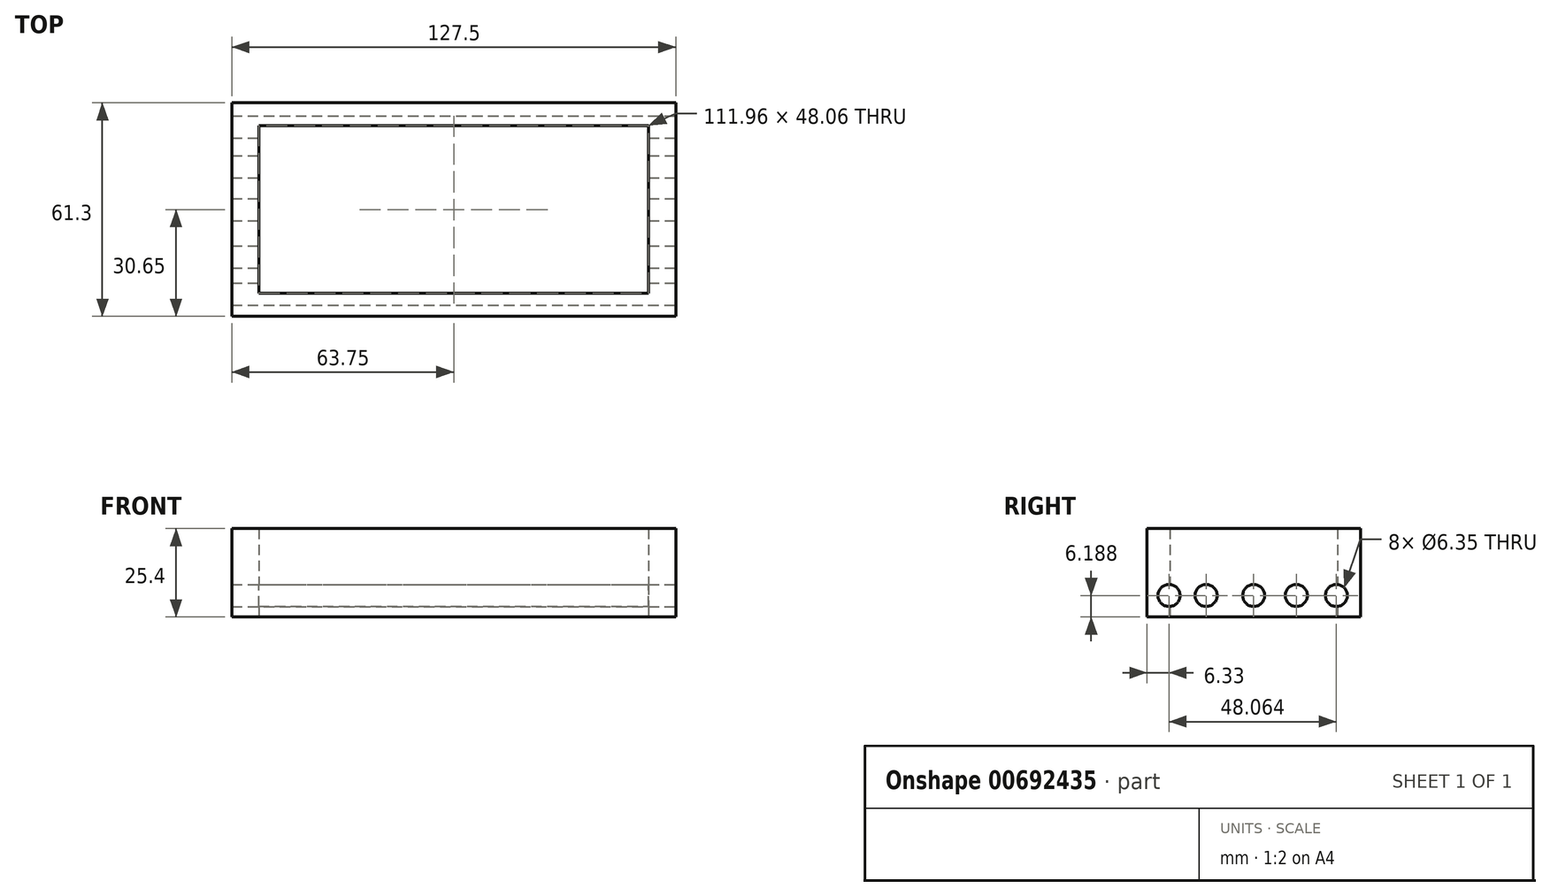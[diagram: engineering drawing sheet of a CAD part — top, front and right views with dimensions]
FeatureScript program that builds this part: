
annotation { "Feature Type Name" : "Feature", "Feature Type Description" : "" }
export const myFeature = defineFeature(function(context is Context, id is Id, definition is map)
    precondition{}
    {
        {
            var Q0;
            Q0=qCreatedBy(makeId("Top.planeOp"),FACE);
            var sketch = newSketch(context, id + "F0", { "sketchPlane" : qUnion([Q0])});
            skLineSegment(sketch, "E0.bottom", {"start": v(-63.75, 30.65) * mm, "end": v(63.75, 30.65) * mm});
            skLineSegment(sketch, "E0.top", {"start": v(-63.75, -30.65) * mm, "end": v(63.75, -30.65) * mm});
            skLineSegment(sketch, "E0.left", {"start": v(-63.75, 30.65) * mm, "end": v(-63.75, -30.65) * mm});
            skLineSegment(sketch, "E0.right", {"start": v(63.75, 30.65) * mm, "end": v(63.75, -30.65) * mm});
            skPoint(sketch, "E0.middle", {"position": v(0, 0) * mm});
            skLineSegment(sketch, "E1.bottom", {"start": v(-55.98, 24.03) * mm, "end": v(55.98, 24.03) * mm});
            skLineSegment(sketch, "E1.top", {"start": v(-55.98, -24.03) * mm, "end": v(55.98, -24.03) * mm});
            skLineSegment(sketch, "E1.left", {"start": v(-55.98, 24.03) * mm, "end": v(-55.98, -24.03) * mm});
            skLineSegment(sketch, "E1.right", {"start": v(55.98, 24.03) * mm, "end": v(55.98, -24.03) * mm});
            skSolve(sketch);
        }
        {
            var Q0;
            Q0=makeQuery(id+"F0.imprint","IMPRINT",FACE,{"disambiguationData":[TD([[makeQuery(id+"F0.imprint","IMPRINT",EDGE,{"derivedFrom":sQuery(id+"F0.wireOp",EDGE,"E0.bottom")}),-1.0]])]});
            extrude(context, id + "F1", {"entities" : qUnion([Q0]), "depth" : 25.4 * mm, "offsetDistance" : 25.4 * mm});
        }
        {
            var Q0;
            Q0=makeQuery(id+"F1.opExtrude","SWEPT_FACE",FACE,{"disambiguationData":[OSD([sQuery(id+"F0.wireOp",EDGE,"E0.right")])]});
            var sketch = newSketch(context, id + "F2", { "sketchPlane" : qUnion([Q0])});
            skPoint(sketch, "E2", {"position": v(-24.32, 6.19) * mm});
            skPoint(sketch, "E3", {"position": v(-13.67, 6.19) * mm});
            skPoint(sketch, "E4", {"position": v(0, 6.19) * mm});
            skPoint(sketch, "E5", {"position": v(12.23, 6.19) * mm});
            skPoint(sketch, "E6", {"position": v(23.74, 6.19) * mm});
            skSolve(sketch);
        }
        {
            var Q0;
            Q0=sQuery(id+"F2.wireOp",VERTEX,"E2");
            var Q1;
            Q1=sQuery(id+"F2.wireOp",VERTEX,"E3");
            var Q2;
            Q2=sQuery(id+"F2.wireOp",VERTEX,"E4");
            var Q3;
            Q3=sQuery(id+"F2.wireOp",VERTEX,"E5");
            var Q4;
            Q4=sQuery(id+"F2.wireOp",VERTEX,"E6");
            var Q5;
            Q5=makeQuery(id+"F1.opExtrude","SWEPT_BODY",BODY,{"disambiguationData":[OSD([sQuery(id+"F0.wireOp",EDGE,"E0.bottom"),sQuery(id+"F0.wireOp",EDGE,"E0.top"),sQuery(id+"F0.wireOp",EDGE,"E0.left"),sQuery(id+"F0.wireOp",EDGE,"E0.right"),sQuery(id+"F0.wireOp",EDGE,"E1.bottom"),sQuery(id+"F0.wireOp",EDGE,"E1.top"),sQuery(id+"F0.wireOp",EDGE,"E1.left"),sQuery(id+"F0.wireOp",EDGE,"E1.right")])]});
            hole(context, id + "F3", {"style" : HoleStyle.SIMPLE, "endStyle" : HoleEndStyle.THROUGH, "holeDiameter" : 6.35 * mm, "majorDiameter" : 6.35 * mm, "isTappedThrough" : true, "tappedDepth" : 12.7 * mm, "tapClearance" : 3, "locations" : qUnion([Q0, Q1, Q2, Q3, Q4]), "scope" : qUnion([Q5])});
        }
    });
